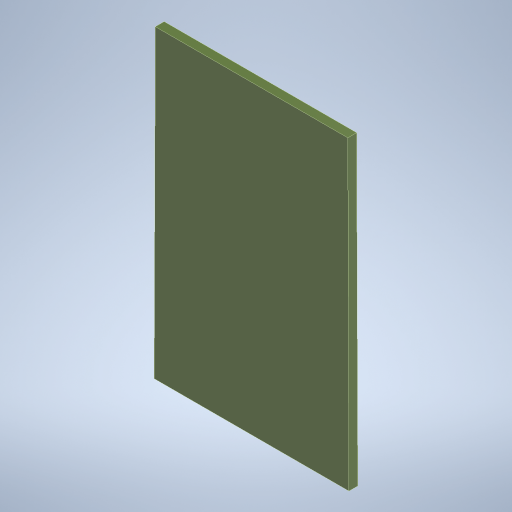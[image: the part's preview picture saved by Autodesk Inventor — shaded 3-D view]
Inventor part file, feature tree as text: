
AUTODESK INVENTOR PART (.ipt)
format: ipt  version: 2024.3 (Build 283343000, 343)  size: 223,232 bytes
history: native  units: mm
features: extrude x1, sketch x1
ambient origin geometry x8: Origin, YZ Plane, XZ Plane, XY Plane, X Axis, Y Axis, Z Axis, Center Point
bodies: Solid1 (feature_tree)
feature tree (2):
  extrude  "Extrusion1"  Depth=69.0mm
  sketch  "Sketch1"  dims[d0=43.5mm d1=69.0mm d2=44.0mm d3=69.0mm d4=2.0mm d5=0.0mm]
